# Revit family: CRV-CSALR1CLRRBA
name_source: partatom
category: Lighting Fixtures
units: mm (PartAtom-declared; Revit-internal decimal feet)

## family parameters
Cut with Voids When Loaded = No
Host = Face
Light Source = No
Maintain Annotation Orientation = No
Part Type = Normal
Room Calculation Point = No
Round Connector Dimension = Use Diameter
Shared = No

## types (1)
- CRV-CSALR1CLRRBA
    Default Elevation = 4' - 0"
    Description = The CURVA COMBO (CRV-C) combines the architectural design of an 
edge-lit exit sign with fully adjustable, high-output, recessed 
emergency LED lamp heads for a modern, sleek, aesthetic appeal. The 
CRV-C achieves up to 66' on-center spacing and is ideal for offices, 
classrooms, corridors, lobbies, and other indoor commercial spaces 
requiring a minimalist aesthetic with high performance emergency 
lighting.
    FACE MATERIAL = Face material
    HOUSING MATERIAL = HOUSING MATERIAL
    LED MATERIAL = LED MATERIAL
    LETTER MATERIAL = LETTERS MATERIAL
    Lamp = LED
    Manufacturer = BEGHELLI
    Model = CURVA COMBO
    Type Comments = EMERGENCY LIGHTING
    Type Image = CURVA COMBO RECESSED IMAGE.PNG
    Wattage Comments = 2 x 1.5W

## geometry (parser evidence)
native form markers: Sweep x8
no freeform markers — native parametric forms only
